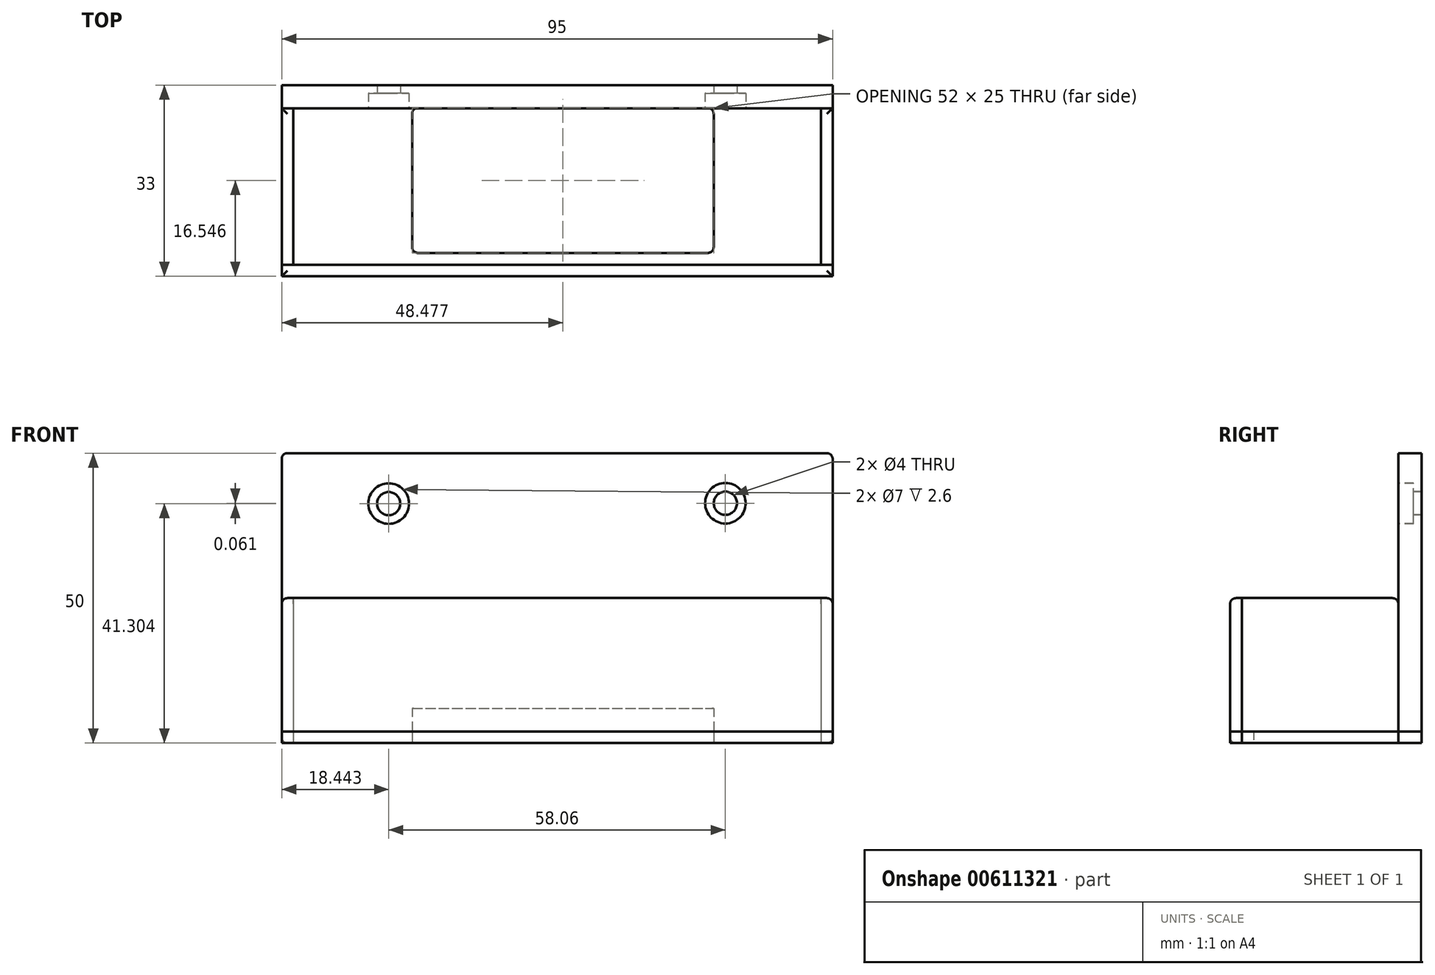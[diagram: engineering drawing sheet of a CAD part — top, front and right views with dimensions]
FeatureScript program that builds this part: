
annotation { "Feature Type Name" : "Feature", "Feature Type Description" : "" }
export const myFeature = defineFeature(function(context is Context, id is Id, definition is map)
    precondition{}
    {
        {
            var Q0;
            Q0=qCreatedBy(makeId("Top.planeOp"),FACE);
            var sketch = newSketch(context, id + "F0", { "sketchPlane" : qUnion([Q0])});
            skLineSegment(sketch, "E0.bottom", {"start": v(47.5, -16.5) * mm, "end": v(-47.5, -16.5) * mm});
            skLineSegment(sketch, "E0.top", {"start": v(47.5, 16.5) * mm, "end": v(-47.5, 16.5) * mm});
            skLineSegment(sketch, "E0.left", {"start": v(47.5, -16.5) * mm, "end": v(47.5, 16.5) * mm});
            skLineSegment(sketch, "E0.right", {"start": v(-47.5, -16.5) * mm, "end": v(-47.5, 16.5) * mm});
            skPoint(sketch, "E0.middle", {"position": v(0, 0) * mm});
            skSolve(sketch);
        }
        {
            var Q0;
            Q0 = qSketchRegion(id + "F0", true);
            extrude(context, id + "F1", {"entities" : qUnion([Q0]), "depth" : 2 * mm, "offsetDistance" : 25 * mm});
        }
        {
            var Q0;
            Q0=makeQuery(id+"F0.imprint","IMPRINT",FACE,{"disambiguationData":[TD([[makeQuery(id+"F0.imprint","IMPRINT",EDGE,{"derivedFrom":sQuery(id+"F0.wireOp",EDGE,"E0.bottom")}),-1.0]])]});
            var sketch = newSketch(context, id + "F2", { "sketchPlane" : qUnion([Q0])});
            skLineSegment(sketch, "E1.bottom", {"start": v(-25.02, 12.55) * mm, "end": v(26.98, 12.55) * mm});
            skLineSegment(sketch, "E1.top", {"start": v(-25.02, -12.45) * mm, "end": v(26.98, -12.45) * mm});
            skLineSegment(sketch, "E1.left", {"start": v(-25.02, 12.55) * mm, "end": v(-25.02, -12.45) * mm});
            skLineSegment(sketch, "E1.right", {"start": v(26.98, 12.55) * mm, "end": v(26.98, -12.45) * mm});
            skSolve(sketch);
        }
        {
            var Q0;
            Q0=makeQuery(id+"F0.imprint","IMPRINT",FACE,{"disambiguationData":[TD([[makeQuery(id+"F0.imprint","IMPRINT",EDGE,{"derivedFrom":sQuery(id+"F0.wireOp",EDGE,"E0.bottom")}),-1.0]])]});
            var sketch = newSketch(context, id + "F3", { "sketchPlane" : qUnion([Q0])});
            skLineSegment(sketch, "E2.bottom", {"start": v(-47.5, 16.5) * mm, "end": v(47.5, 16.5) * mm});
            skLineSegment(sketch, "E2.top", {"start": v(-47.5, 12.5) * mm, "end": v(47.5, 12.5) * mm});
            skLineSegment(sketch, "E2.left", {"start": v(-47.5, 16.5) * mm, "end": v(-47.5, 12.5) * mm});
            skLineSegment(sketch, "E2.right", {"start": v(47.5, 16.5) * mm, "end": v(47.5, 12.5) * mm});
            skSolve(sketch);
        }
        {
            var Q0;
            Q0=makeQuery(id+"F0.imprint","IMPRINT",FACE,{"disambiguationData":[TD([[makeQuery(id+"F0.imprint","IMPRINT",EDGE,{"derivedFrom":sQuery(id+"F0.wireOp",EDGE,"E0.bottom")}),-1.0]])]});
            var sketch = newSketch(context, id + "F4", { "sketchPlane" : qUnion([Q0])});
            skLineSegment(sketch, "E3.bottom", {"start": v(-47.5, -16.5) * mm, "end": v(47.5, -16.5) * mm});
            skLineSegment(sketch, "E3.top", {"start": v(-47.5, -14.5) * mm, "end": v(47.5, -14.5) * mm});
            skLineSegment(sketch, "E3.left", {"start": v(-47.5, -16.5) * mm, "end": v(-47.5, -14.5) * mm});
            skLineSegment(sketch, "E3.right", {"start": v(47.5, -16.5) * mm, "end": v(47.5, -14.5) * mm});
            skSolve(sketch);
        }
        {
            var Q0;
            Q0=makeQuery(id+"F0.imprint","IMPRINT",FACE,{"disambiguationData":[TD([[makeQuery(id+"F0.imprint","IMPRINT",EDGE,{"derivedFrom":sQuery(id+"F0.wireOp",EDGE,"E0.bottom")}),-1.0]])]});
            var sketch = newSketch(context, id + "F5", { "sketchPlane" : qUnion([Q0])});
            skLineSegment(sketch, "E4.bottom", {"start": v(-47.5, 12.5) * mm, "end": v(-45.5, 12.5) * mm});
            skLineSegment(sketch, "E4.top", {"start": v(-47.5, -14.5) * mm, "end": v(-45.5, -14.5) * mm});
            skLineSegment(sketch, "E4.left", {"start": v(-47.5, 12.5) * mm, "end": v(-47.5, -14.5) * mm});
            skLineSegment(sketch, "E4.right", {"start": v(-45.5, 12.5) * mm, "end": v(-45.5, -14.5) * mm});
            skSolve(sketch);
        }
        {
            var Q0;
            Q0=makeQuery(id+"F0.imprint","IMPRINT",FACE,{"disambiguationData":[TD([[makeQuery(id+"F0.imprint","IMPRINT",EDGE,{"derivedFrom":sQuery(id+"F0.wireOp",EDGE,"E0.bottom")}),-1.0]])]});
            var sketch = newSketch(context, id + "F6", { "sketchPlane" : qUnion([Q0])});
            skLineSegment(sketch, "E5.bottom", {"start": v(47.5, 12.5) * mm, "end": v(45.5, 12.5) * mm});
            skLineSegment(sketch, "E5.top", {"start": v(47.5, -14.5) * mm, "end": v(45.5, -14.5) * mm});
            skLineSegment(sketch, "E5.left", {"start": v(47.5, 12.5) * mm, "end": v(47.5, -14.5) * mm});
            skLineSegment(sketch, "E5.right", {"start": v(45.5, 12.5) * mm, "end": v(45.5, -14.5) * mm});
            skSolve(sketch);
        }
        {
            var Q0;
            Q0 = qSketchRegion(id + "F4", true);
            var Q1;
            Q1 = qSketchRegion(id + "F5", true);
            var Q2;
            Q2 = qSketchRegion(id + "F6", true);
            extrude(context, id + "F7", {"entities" : qUnion([Q0, Q1, Q2]), "depth" : 25 * mm, "offsetDistance" : 25 * mm});
        }
        {
            var Q0;
            Q0 = qSketchRegion(id + "F3", true);
            extrude(context, id + "F8", {"entities" : qUnion([Q0]), "depth" : 50 * mm, "offsetDistance" : 25 * mm});
        }
        {
            var Q0;
            Q0 = qSketchRegion(id + "F2", true);
            extrude(context, id + "F9", {"entities" : qUnion([Q0]), "operationType" : NewBodyOperationType.REMOVE, "depth" : 6 * mm, "offsetDistance" : 25 * mm});
        }
        {
            var Q0;
            Q0=makeQuery(id+"F8.opExtrude","CAP_EDGE",EDGE,{"disambiguationData":[OSD([sQuery(id+"F3.wireOp",EDGE,"E2.right")])],"isStart":false});
            var Q1;
            Q1=makeQuery(id+"F8.opExtrude","CAP_EDGE",EDGE,{"disambiguationData":[OSD([sQuery(id+"F3.wireOp",EDGE,"E2.left")])],"isStart":false});
            var Q2;
            Q2=makeQuery(id+"F8.opExtrude","CAP_EDGE",EDGE,{"disambiguationData":[OSD([sQuery(id+"F3.wireOp",EDGE,"E2.left")])],"isStart":true});
            var Q3;
            Q3=makeQuery(id+"F1.opExtrude","CAP_EDGE",EDGE,{"disambiguationData":[OSD([sQuery(id+"F0.wireOp",EDGE,"E0.right")])],"isStart":true});
            var Q4;
            Q4=makeQuery(id+"F1.opExtrude","CAP_EDGE",EDGE,{"disambiguationData":[OSD([sQuery(id+"F0.wireOp",EDGE,"E0.left")])],"isStart":true});
            var Q5;
            Q5=makeQuery(id+"F1.opExtrude","CAP_EDGE",EDGE,{"disambiguationData":[OSD([sQuery(id+"F0.wireOp",EDGE,"E0.bottom")])],"isStart":true});
            var Q6;
            Q6=makeQuery(id+"F7.opExtrude","CAP_EDGE",EDGE,{"disambiguationData":[OSD([sQuery(id+"F5.wireOp",EDGE,"E4.bottom")])],"isStart":false});
            var Q7;
            Q7=makeQuery(id+"F7.opExtrude","CAP_EDGE",EDGE,{"disambiguationData":[OSD([sQuery(id+"F6.wireOp",EDGE,"E5.bottom")])],"isStart":false});
            var Q8;
            Q8=makeQuery(id+"F7.opExtrude","CAP_EDGE",EDGE,{"disambiguationData":[OSD([sQuery(id+"F4.wireOp",EDGE,"E3.bottom")])],"isStart":false});
            var Q9;
            Q9=makeQuery(id+"F7.opExtrude","CAP_EDGE",EDGE,{"disambiguationData":[OSD([sQuery(id+"F5.wireOp",EDGE,"E4.left")])],"isStart":false});
            var Q10;
            Q10=makeQuery(id+"F7.opExtrude","CAP_EDGE",EDGE,{"disambiguationData":[OSD([sQuery(id+"F4.wireOp",EDGE,"E3.left")])],"isStart":false});
            var Q11;
            Q11=makeQuery(id+"F7.opExtrude","CAP_EDGE",EDGE,{"disambiguationData":[OSD([sQuery(id+"F4.wireOp",EDGE,"E3.right")])],"isStart":false});
            var Q12;
            Q12=makeQuery(id+"F7.opExtrude","CAP_EDGE",EDGE,{"disambiguationData":[OSD([sQuery(id+"F6.wireOp",EDGE,"E5.left")])],"isStart":false});
            var Q13;
            Q13=makeQuery(id+"F9.boolean.opBoolean","COPY",EDGE,{"derivedFrom":makeQuery(id+"F9.opExtrude","SWEPT_EDGE",EDGE,{"disambiguationData":[OSD([sQuery(id+"F2.wireOp",EDGE,"E1.top"),sQuery(id+"F2.wireOp",EDGE,"E1.left")])]})});
            var Q14;
            Q14=makeQuery(id+"F9.boolean.opBoolean","COPY",EDGE,{"derivedFrom":makeQuery(id+"F9.opExtrude","SWEPT_EDGE",EDGE,{"disambiguationData":[OSD([sQuery(id+"F2.wireOp",EDGE,"E1.top"),sQuery(id+"F2.wireOp",EDGE,"E1.right")])]})});
            var Q15;
            Q15=makeQuery(id+"F9.boolean.opBoolean","COPY",EDGE,{"derivedFrom":makeQuery(id+"F9.opExtrude","SWEPT_EDGE",EDGE,{"disambiguationData":[OSD([sQuery(id+"F2.wireOp",EDGE,"E1.bottom"),sQuery(id+"F2.wireOp",EDGE,"E1.right")])]})});
            var Q16;
            Q16=makeQuery(id+"F9.boolean.opBoolean","COPY",EDGE,{"derivedFrom":makeQuery(id+"F9.opExtrude","SWEPT_EDGE",EDGE,{"disambiguationData":[OSD([sQuery(id+"F2.wireOp",EDGE,"E1.bottom"),sQuery(id+"F2.wireOp",EDGE,"E1.left")])]})});
            fillet(context, id + "F10", {"entities" : qUnion([Q0, Q1, Q2, Q3, Q4, Q5, Q6, Q7, Q8, Q9, Q10, Q11, Q12, Q13, Q14, Q15, Q16]), "radius" : 1 * mm, "tangentPropagation" : true, "allowEdgeOverflow" : false});
        }
        {
            var Q0;
            Q0=makeQuery(id+"F8.opExtrude","SWEPT_FACE",FACE,{"disambiguationData":[OSD([sQuery(id+"F3.wireOp",EDGE,"E2.top")])]});
            var sketch = newSketch(context, id + "F11", { "sketchPlane" : qUnion([Q0])});
            skCircle(sketch, "E6", {"center": v(-29.06, 41.3) * mm, "radius": 2 * mm});
            skCircle(sketch, "E7", {"center": v(29, 41.37) * mm, "radius": 2 * mm});
            skSolve(sketch);
        }
        {
            var Q0;
            Q0 = qSketchRegion(id + "F11", true);
            extrude(context, id + "F12", {"entities" : qUnion([Q0]), "operationType" : NewBodyOperationType.REMOVE, "oppositeDirection" : true, "depth" : 4 * mm, "offsetDistance" : 25 * mm});
        }
        {
            var Q0;
            Q0=makeQuery(id+"F11.imprint","IMPRINT",FACE,{"disambiguationData":[TD([[makeQuery(id+"F11.imprint","IMPRINT",EDGE,{"derivedFrom":sQuery(id+"F11.wireOp",EDGE,"E6")}),-1.0]])]});
            var sketch = newSketch(context, id + "F13", { "sketchPlane" : qUnion([Q0])});
            skCircle(sketch, "E8", {"center": v(-29.06, 41.3) * mm, "radius": 3.5 * mm});
            skCircle(sketch, "E9", {"center": v(29, 41.37) * mm, "radius": 3.5 * mm});
            skSolve(sketch);
        }
        {
            var Q0;
            Q0 = qSketchRegion(id + "F13", true);
            extrude(context, id + "F14", {"entities" : qUnion([Q0]), "operationType" : NewBodyOperationType.REMOVE, "oppositeDirection" : true, "depth" : 2.6 * mm, "offsetDistance" : 25 * mm});
        }
    });
